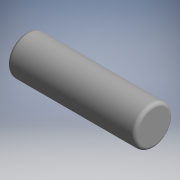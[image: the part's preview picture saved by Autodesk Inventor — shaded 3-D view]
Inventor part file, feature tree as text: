
AUTODESK INVENTOR PART (.ipt)
format: ipt  version: 2017.3 (Build 213256000, 256)  size: 97,280 bytes
history: native  units: mm (DEFAULTED — no unit token found)
features: other x7, revolve x1, sketch x1
ambient origin geometry x8: Origin, YZ Plane, XZ Plane, XY Plane, X Axis, Y Axis, Z Axis, Center Point
bodies: Solid1 (feature_tree)
feature tree (9):
  revolve  "Revolution1"  [1 undecoded]
  other  "IP_1_XY"
  other  "IP_1_YZ"
  other  "IP_1_ZX"
  other  "IP_1_X"
  other  "IP_1_Y"
  other  "IP_1_Z"
  other  "IP_1_Center"
  sketch  "Sketch_1"  dims[d0=360.0deg]
note: 1 required parameter value undecoded (feature->parameter linkage not recoverable at this tier; creation-order binding heuristic only, values carry confidence <= 0.55)
